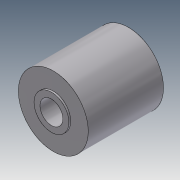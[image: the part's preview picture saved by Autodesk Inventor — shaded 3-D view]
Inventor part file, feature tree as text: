
AUTODESK INVENTOR PART (.ipt)
format: ipt  version: 2018.3 (Build 223284000, 284)  size: 110,080 bytes
history: native  units: in
note: dims shown in document units (in); Inventor stores cm internally (conversion verified against a paired STEP export)
features: extrude x2, sketch x2, projected_geometry x1
ambient origin geometry x8: Origin, YZ Plane, XZ Plane, XY Plane, X Axis, Y Axis, Z Axis, Center Point
bodies: Solid1 (feature_tree)
feature tree (5):
  extrude  "Extrusion1"  Depth=1.5in
  extrude  "Extrusion2"  Depth=0.04in
  sketch  "Sketch1"  dims[d0=0.4921in d1=1.5in]
  sketch  "Sketch2"  dims[d2=1.656in d3=0.0in d4=0.748in d5=0.04in d6=0.0in]
  projected_geometry  "Projected Loop1"
